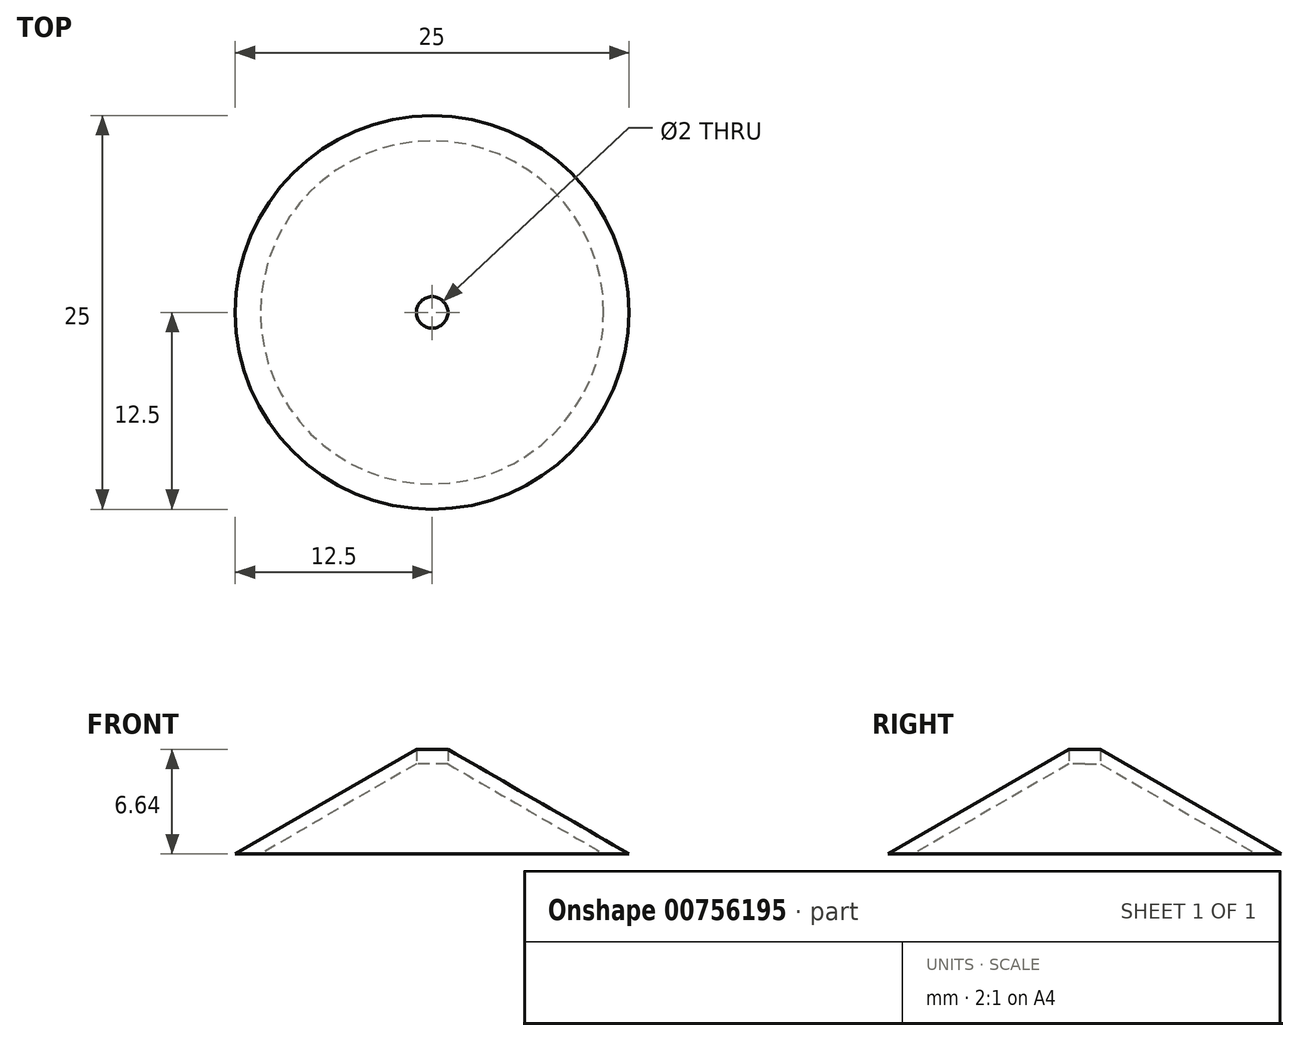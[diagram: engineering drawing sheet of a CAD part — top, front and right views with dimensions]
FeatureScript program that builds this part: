
annotation { "Feature Type Name" : "Feature", "Feature Type Description" : "" }
export const myFeature = defineFeature(function(context is Context, id is Id, definition is map)
    precondition{}
    {
        {
            var Q0;
            Q0=qCreatedBy(makeId("Top.planeOp"),FACE);
            var sketch = newSketch(context, id + "F0", { "sketchPlane" : qUnion([Q0])});
            skCircle(sketch, "E0", {"center": v(0, 0) * mm, "radius": 12.5 * mm});
            skSolve(sketch);
        }
        {
            var Q0;
            Q0=makeQuery(id+"F0.imprint","IMPRINT",FACE,{"disambiguationData":[TD([[makeQuery(id+"F0.imprint","IMPRINT",EDGE,{"derivedFrom":sQuery(id+"F0.wireOp",EDGE,"E0")}),1.0]])]});
            extrude(context, id + "F1", {"entities" : qUnion([Q0]), "depth" : 7.5 * mm, "offsetDistance" : 25 * mm, "hasDraft" : true, "draftAngle" : 60 * degree, "draftPullDirection" : true});
        }
        {
            var Q0;
            Q0=qCreatedBy(makeId("Top.planeOp"),FACE);
            var sketch = newSketch(context, id + "F2", { "sketchPlane" : qUnion([Q0])});
            skCircle(sketch, "E1", {"center": v(0, 0) * mm, "radius": 1 * mm});
            skSolve(sketch);
        }
        {
            var Q0;
            Q0=makeQuery(id+"F1.opExtrude","CAP_FACE",FACE,{"disambiguationData":[OSD([sQuery(id+"F0.wireOp",EDGE,"E0")])],"isStart":true});
            shell(context, id + "F3", {"entities" : qUnion([Q0]), "thickness" : 0.8 * mm});
        }
        {
            var Q0;
            Q0 = qSketchRegion(id + "F2", true);
            extrude(context, id + "F4", {"entities" : qUnion([Q0]), "operationType" : NewBodyOperationType.REMOVE, "depth" : 25 * mm, "offsetDistance" : 25 * mm});
        }
    });
